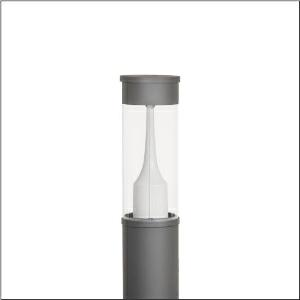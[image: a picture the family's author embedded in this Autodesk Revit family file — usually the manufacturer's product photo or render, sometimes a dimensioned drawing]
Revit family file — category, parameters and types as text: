
# Revit family: city-light_120_iq___pl1_2s_5xa5285of14h_ee05
name_source: partatom
category: Lighting Fixtures
units: mm (PartAtom-declared; Revit-internal decimal feet)

## family parameters
Cut with Voids When Loaded = No
Host = Face
Light Source = No
Part Type = Normal
Room Calculation Point = No
Round Connector Dimension = Use Diameter
Shared = No

## types (1)
- --- (1 x LED, 2970 lm, 21.8 W, 2700K)
    Apparent Load = 22 VA
    CIE Flux Codes = 23 62 94 96 100
    Color Rendering = 70
    Color Temperature = 2700K
    Default Elevation = 1800 mm
    Description = City-Light 120 iQ, bollard luminaire, Module 540 iQ-SR, primary light control with 3 zone facetted reflector, of plastic, silver coated, highly specular, structured, primary optical cover: cover, of PMMA, transparent, partly coated, light distribution: PL1.2s, primary light characteristic: symmetric, LED, High Power LED, rated luminous flux: 2.970lm, luminous efficacy: 136lm/W, light colour: 727, colour temperature: 2700K, control gear: ECG iQ, control: pre-setting: logarithmic dimming characteristic, Street-Remote, Auto-Match, Temp-Guard, Lumen-Switch, Night-Set, Smart-Wire, Light-Fading, Desk-Remote (wireless, voltage-free reading and setting of iQ features in the workshop via application-optimized NFC function/RFID function), optimised constant luminous flux control (CLO 2.0), with terminal, 6-pole, max. 2.5mm², mains connection: 230..240V, AC, 50/60Hz, start of lifetime: 22W, end of service life: 23W, reduction: 11W, luminaire housing, cylindrical, of extruded aluminium section, coated, Siteco® metallic grey (DB 702S), length: 1.200mm, diameter: 200mm, Module 540 iQ-SR, traffic white (RAL 9016), equipment: standard, protection rating (complete): IP54, insulation class (complete): insulation class II (safety insulation), certification: CE, ENEC, VDE, packaging unit: 1 piece

Light Distribution: PL1.2s
    Height = 500 mm
    Lamp = 1 x LED
    Lamp Light Flux = 2970 lm
    Lamp Power = 21.8 W
    Lamp count = 1
    Length = 200 mm  [stored 0.656168 ft]
    Luminous efficacy = 136 lm/W
    Manufacturer = Siteco
    ModVariant = No
    Model = 5XA5285OF14H
    Mounting Place = Floor
    Mounting Type = Freestanding
    Number of Poles = 1
    OnlyDefault = Yes
    Power Factor = 1
    Product Name = City-Light 120 iQ | PL1.2s
    Product group = bollard luminaire
    ProductGroupID = 1304
    Protection Class = Protection class II
    Protection Degree = IP 54
    RLX_Detail_Level = 1
    RLX_Emergency_Light_Flux = 0 lm
    RLX_Emergency_Type = 0
    RLX_Emergency_Type_DB = No
    RlxData = <blob elided: 30141 chars, md5=b3fe5f2a>
    Socket = socket
    Standby Power = 0 W
    System Light Flux = 2970 lm
    System Power = 22 W
    Type Comments = factory setting: luminous flux: 100 % | dim-lin: 254 | 456 mA
    Type Image = l_1006922.jpg
    URL = http://relux.com
    VarID = @adj_115051
    Voltage = 0 V
    Weight = 0.00 kg
    Width = 0 mm  [stored 0 ft]

note: [stored X ft] marks values corroborated as IEEE doubles in the binary element streams (Revit-internal decimal feet)

## geometry (parser evidence)
native form markers: Blend x4, Sweep x10
no freeform markers — native parametric forms only
